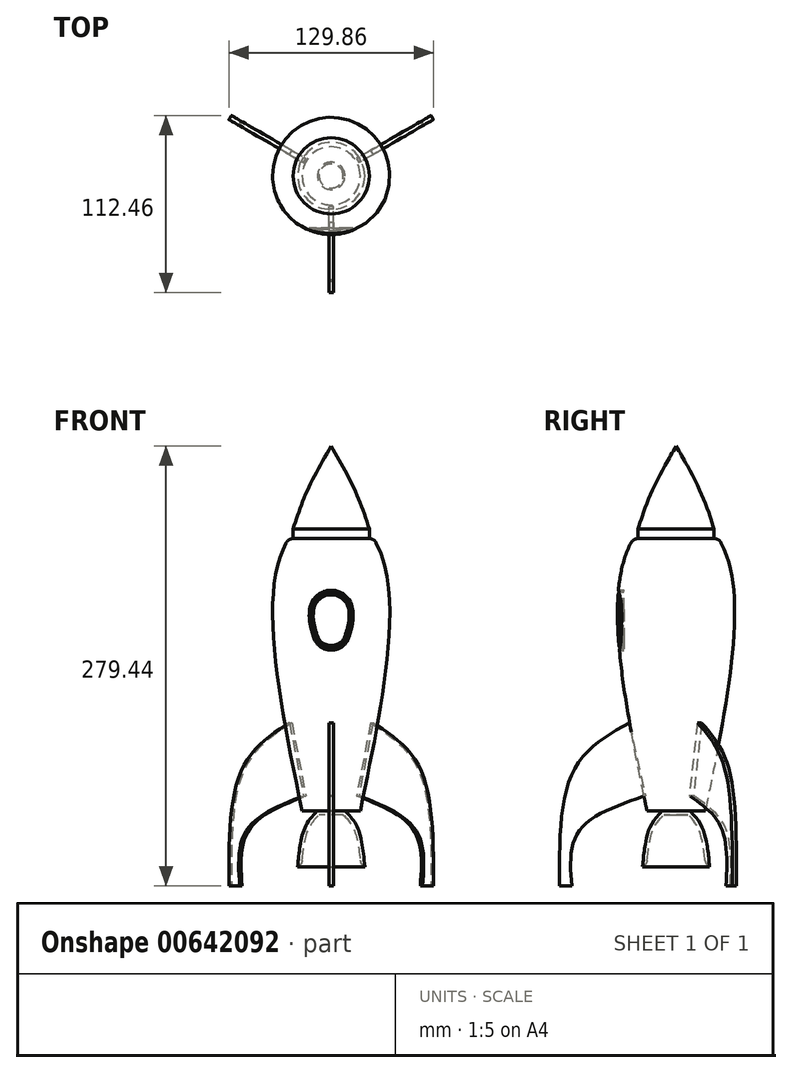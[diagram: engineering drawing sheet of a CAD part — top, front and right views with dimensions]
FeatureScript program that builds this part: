
annotation { "Feature Type Name" : "Feature", "Feature Type Description" : "" }
export const myFeature = defineFeature(function(context is Context, id is Id, definition is map)
    precondition{}
    {
        {
            var Q0;
            Q0=qCreatedBy(makeId("Front.planeOp"),FACE);
            var sketch = newSketch(context, id + "F0", { "sketchPlane" : qUnion([Q0])});
            skLineSegment(sketch, "E0", {"start": v(-18.47, -47.16) * mm, "end": v(0, -47.16) * mm});
            skLineSegment(sketch, "E1", {"start": v(0, -47.16) * mm, "end": v(0, 125.99) * mm});
            skFitSpline(sketch, "E2.trimOffspring", {"points": [v(0, 156.26) * mm, v(-33.74, 109.9) * mm, v(-18.47, -47.16) * mm], "startDerivative": vector(-111.18, -99.1) * mm, "endDerivative": vector(60.1, -291.82) * mm});
            skLineSegment(sketch, "E3", {"start": v(-27.12, 125.99) * mm, "end": v(0, 125.99) * mm});
            skSolve(sketch);
        }
        {
            var Q0;
            Q0=qCreatedBy(makeId("Front.planeOp"),FACE);
            var sketch = newSketch(context, id + "F1", { "sketchPlane" : qUnion([Q0])});
            skFitSpline(sketch, "E4", {"points": [v(-8.7, -46.94) * mm, v(-16.73, -57.72) * mm, v(-21.31, -82.48) * mm], "startDerivative": vector(-21.35, -21.88) * mm, "endDerivative": vector(-4.74, -47.86) * mm});
            skLineSegment(sketch, "E5", {"start": v(-8.7, -46.94) * mm, "end": v(0, -46.94) * mm});
            skLineSegment(sketch, "E6", {"start": v(0, -46.94) * mm, "end": v(0, -79.73) * mm});
            skLineSegment(sketch, "E7", {"start": v(0, -79.73) * mm, "end": v(-21.31, -82.48) * mm});
            skSolve(sketch);
        }
        {
            var Q0;
            Q0=makeQuery(id+"F1.imprint","IMPRINT",FACE,{"disambiguationData":[TD([[makeQuery(id+"F1.imprint","IMPRINT",EDGE,{"derivedFrom":sQuery(id+"F1.wireOp",EDGE,"E4")}),1.0]])]});
            var Q1;
            Q1=sQuery(id+"F1.wireOp",EDGE,"E6");
            revolve(context, id + "F2", {"entities" : qUnion([Q0]), "axis" : qUnion([Q1]), "revolveType" : RevolveType.FULL});
        }
        {
            var Q0;
            Q0=makeQuery(id+"F2.opRevolve","SWEPT_FACE",FACE,{"disambiguationData":[OSD([sQuery(id+"F1.wireOp",EDGE,"E7")])]});
            shell(context, id + "F3", {"entities" : qUnion([Q0]), "thickness" : 2.5 * mm});
        }
        {
            var Q0;
            Q0=qCreatedBy(makeId("Right.planeOp"),FACE);
            var sketch = newSketch(context, id + "F4", { "sketchPlane" : qUnion([Q0])});
            skFitSpline(sketch, "E8", {"points": [v(-29.75, 9) * mm, v(-64.45, -20.3) * mm, v(-74.1, -94.73) * mm], "startDerivative": vector(-92.92, -52.68) * mm, "endDerivative": vector(0.34, -150.7) * mm});
            skLineSegment(sketch, "E9", {"start": v(0, 24.92) * mm, "end": v(0, -98.6) * mm, "construction": true});
            skFitSpline(sketch, "E10", {"points": [v(-66.2, -95.36) * mm, v(-62.02, -60.36) * mm, v(-21.04, -37.93) * mm], "startDerivative": vector(-6.7, 83.04) * mm, "endDerivative": vector(94.64, 32.99) * mm});
            skLineSegment(sketch, "E11", {"start": v(-29.75, 9) * mm, "end": v(-19.48, -37.46) * mm});
            skLineSegment(sketch, "E12", {"start": v(-74.1, -94.73) * mm, "end": v(-66.25, -94.73) * mm});
            skLineSegment(sketch, "E13", {"start": v(-21.04, -37.93) * mm, "end": v(-19.48, -37.46) * mm});
            skPoint(sketch, "E14.orphan", {"position": v(-19.38, -37.93) * mm});
            skSolve(sketch);
        }
        {
            var Q0;
            Q0=makeQuery(id+"F4.imprint","IMPRINT",FACE,{"disambiguationData":[TD([[makeQuery(id+"F4.imprint","IMPRINT",EDGE,{"derivedFrom":sQuery(id+"F4.wireOp",EDGE,"E8")}),1.0]])]});
            extrude(context, id + "F5", {"entities" : qUnion([Q0]), "depth" : 3 * mm, "offsetDistance" : 25 * mm, "symmetric" : true});
        }
        {
            var Q0;
            Q0=makeQuery(id+"F5.opExtrude","SWEPT_BODY",BODY,{"disambiguationData":[OSD([sQuery(id+"F4.wireOp",EDGE,"E8"),sQuery(id+"F4.wireOp",EDGE,"AknD3gLe-WbWz-Pry5-1471-UmxbraZWTH3h"),sQuery(id+"F4.wireOp",EDGE,"97d6337d-07c4-4e44-8112-b2ea29076221")])]});
            var Q1;
            Q1=sQuery(id+"F4.wireOp",EDGE,"E9");
            circularPattern(context, id + "F6", {"entities" : qUnion([Q0]), "axis" : qUnion([Q1]), "angle" : 360 * degree, "instanceCount" : 3, "equalSpace" : true, "computeTransformsWithoutBuiltin" : true});
        }
        {
            var Q0;
            Q0=makeQuery(id+"F0.imprint","IMPRINT",FACE,{"disambiguationData":[TD([[makeQuery(id+"F0.imprint","IMPRINT",EDGE,{"derivedFrom":sQuery(id+"F0.wireOp",EDGE,"E0")}),1.0]])]});
            var Q1;
            Q1=sQuery(id+"F0.wireOp",EDGE,"E1");
            revolve(context, id + "F7", {"entities" : qUnion([Q0]), "axis" : qUnion([Q1]), "revolveType" : RevolveType.FULL});
        }
        {
            var Q0;
            Q0=qCreatedBy(makeId("Front.planeOp"),FACE);
            var sketch = newSketch(context, id + "F8", { "sketchPlane" : qUnion([Q0])});
            skLineSegment(sketch, "E15", {"start": v(-24.2, 126.12) * mm, "end": v(-24.2, 132) * mm});
            skFitSpline(sketch, "E16", {"points": [v(-24.2, 132) * mm, v(-15.43, 155.88) * mm, v(0, 184.7) * mm], "startDerivative": vector(16.27, 50.18) * mm, "endDerivative": vector(31.8, 55.12) * mm});
            skLineSegment(sketch, "E17", {"start": v(0, 184.7) * mm, "end": v(0, 126.3) * mm});
            skLineSegment(sketch, "E18", {"start": v(0, 126.3) * mm, "end": v(-24.2, 126.12) * mm});
            skSolve(sketch);
        }
        {
            var Q0;
            Q0=makeQuery(id+"F8.imprint","IMPRINT",FACE,{"disambiguationData":[TD([[makeQuery(id+"F8.imprint","IMPRINT",EDGE,{"derivedFrom":sQuery(id+"F8.wireOp",EDGE,"E15")}),-1.0]])]});
            var Q1;
            Q1=sQuery(id+"F8.wireOp",EDGE,"E17");
            revolve(context, id + "F9", {"entities" : qUnion([Q0]), "axis" : qUnion([Q1]), "revolveType" : RevolveType.FULL});
        }
        {
            var Q0;
            Q0=qCreatedBy(makeId("Front.planeOp"),FACE);
            cPlane(context, id + "F10", {"entities" : qUnion([Q0]), "cplaneType" : CPlaneType.OFFSET, "offset" : 33 * mm, "width" : 150 * mm, "height" : 150 * mm});
        }
        {
            var Q0;
            Q0=qCreatedBy(id+"F10.planeOp",FACE);
            var sketch = newSketch(context, id + "F11", { "sketchPlane" : qUnion([Q0])});
            skArc(sketch, "E19", {"start": v(12.56, 80.66) * mm, "mid": v(0, 92.05) * mm, "end": v(-12.56, 80.66) * mm});
            skArc(sketch, "E20", {"start": v(-10.2, 63.64) * mm, "mid": v(0, 56.14) * mm, "end": v(10.2, 63.64) * mm});
            skFitSpline(sketch, "E21", {"points": [v(-12.56, 80.66) * mm, v(-12.7, 74.23) * mm, v(-10.2, 63.64) * mm], "startDerivative": vector(-1.32, -13.55) * mm, "endDerivative": vector(5.18, -16.61) * mm});
            skFitSpline(sketch, "E22.MirrorCS", {"points": [v(12.56, 80.66) * mm, v(12.7, 74.23) * mm, v(10.2, 63.64) * mm], "startDerivative": vector(1.32, -13.55) * mm, "endDerivative": vector(-5.18, -16.61) * mm});
            skArc(sketch, "E23.0", {"start": v(13.65, 80.77) * mm, "mid": v(0, 93.15) * mm, "end": v(-13.65, 80.77) * mm});
            skFitSpline(sketch, "E23.1", {"points": [v(13.65, 80.77) * mm, v(13.7, 80.2) * mm, v(13.83, 79.07) * mm, v(13.92, 77.54) * mm, v(13.93, 76.22) * mm, v(13.9, 75.18) * mm, v(13.8, 74.07) * mm, v(13.6, 72.52) * mm, v(13.2, 70.47) * mm, v(12.6, 67.96) * mm, v(11.92, 65.51) * mm, v(11.46, 64) * mm, v(11.24, 63.31) * mm]});
            skArc(sketch, "E23.2", {"start": v(-11.24, 63.31) * mm, "mid": v(0, 55.04) * mm, "end": v(11.24, 63.31) * mm});
            skFitSpline(sketch, "E23.3", {"points": [v(-13.65, 80.77) * mm, v(-13.7, 80.2) * mm, v(-13.83, 79.07) * mm, v(-13.92, 77.54) * mm, v(-13.93, 76.22) * mm, v(-13.9, 75.18) * mm, v(-13.8, 74.07) * mm, v(-13.6, 72.52) * mm, v(-13.2, 70.47) * mm, v(-12.6, 67.96) * mm, v(-11.92, 65.51) * mm, v(-11.46, 64) * mm, v(-11.24, 63.31) * mm]});
            skSolve(sketch);
        }
        {
            var Q0;
            Q0 = qSketchRegion(id + "F11", true);
            extrude(context, id + "F12", {"entities" : qUnion([Q0]), "operationType" : NewBodyOperationType.REMOVE, "endBound" : BoundingType.UP_TO_NEXT, "depth" : 25 * mm, "offsetDistance" : 25 * mm});
        }
        {
            var Q0;
            Q0=makeQuery(id+"F12.boolean.opBoolean","SPLIT",FACE,{"disambiguationData":[TD([makeQuery(id+"F12.opExtrude","SWEPT_FACE",FACE,{"disambiguationData":[OSD([sQuery(id+"F11.wireOp",EDGE,"E19")])]})])],"derivedFrom":makeQuery(id+"F7.opRevolve","SWEPT_FACE",FACE,{"disambiguationData":[OSD([sQuery(id+"F0.wireOp",EDGE,"E2.trimOffspring")])]})});
            fillet(context, id + "F13", {"entities" : qUnion([Q0]), "radius" : 2 * mm, "tangentPropagation" : true, "allowEdgeOverflow" : false});
        }
        {
            var Q0;
            Q0=makeQuery(id+"F7.opRevolve","SWEPT_EDGE",EDGE,{"disambiguationData":[OSD([sQuery(id+"F0.wireOp",EDGE,"E2.trimOffspring"),sQuery(id+"F0.wireOp",EDGE,"E3")])]});
            fillet(context, id + "F14", {"entities" : qUnion([Q0]), "radius" : 5 * mm, "tangentPropagation" : true, "allowEdgeOverflow" : false});
        }
        {
            var Q0;
            Q0=makeQuery(id+"F3.opShell","OFFSET_EDGE",EDGE,{"disambiguationData":[OSD([sQuery(id+"F1.wireOp",EDGE,"E4"),sQuery(id+"F1.wireOp",EDGE,"E7")])]});
            fillet(context, id + "F15", {"entities" : qUnion([Q0]), "radius" : 5 * mm, "tangentPropagation" : true, "allowEdgeOverflow" : false});
        }
    });
